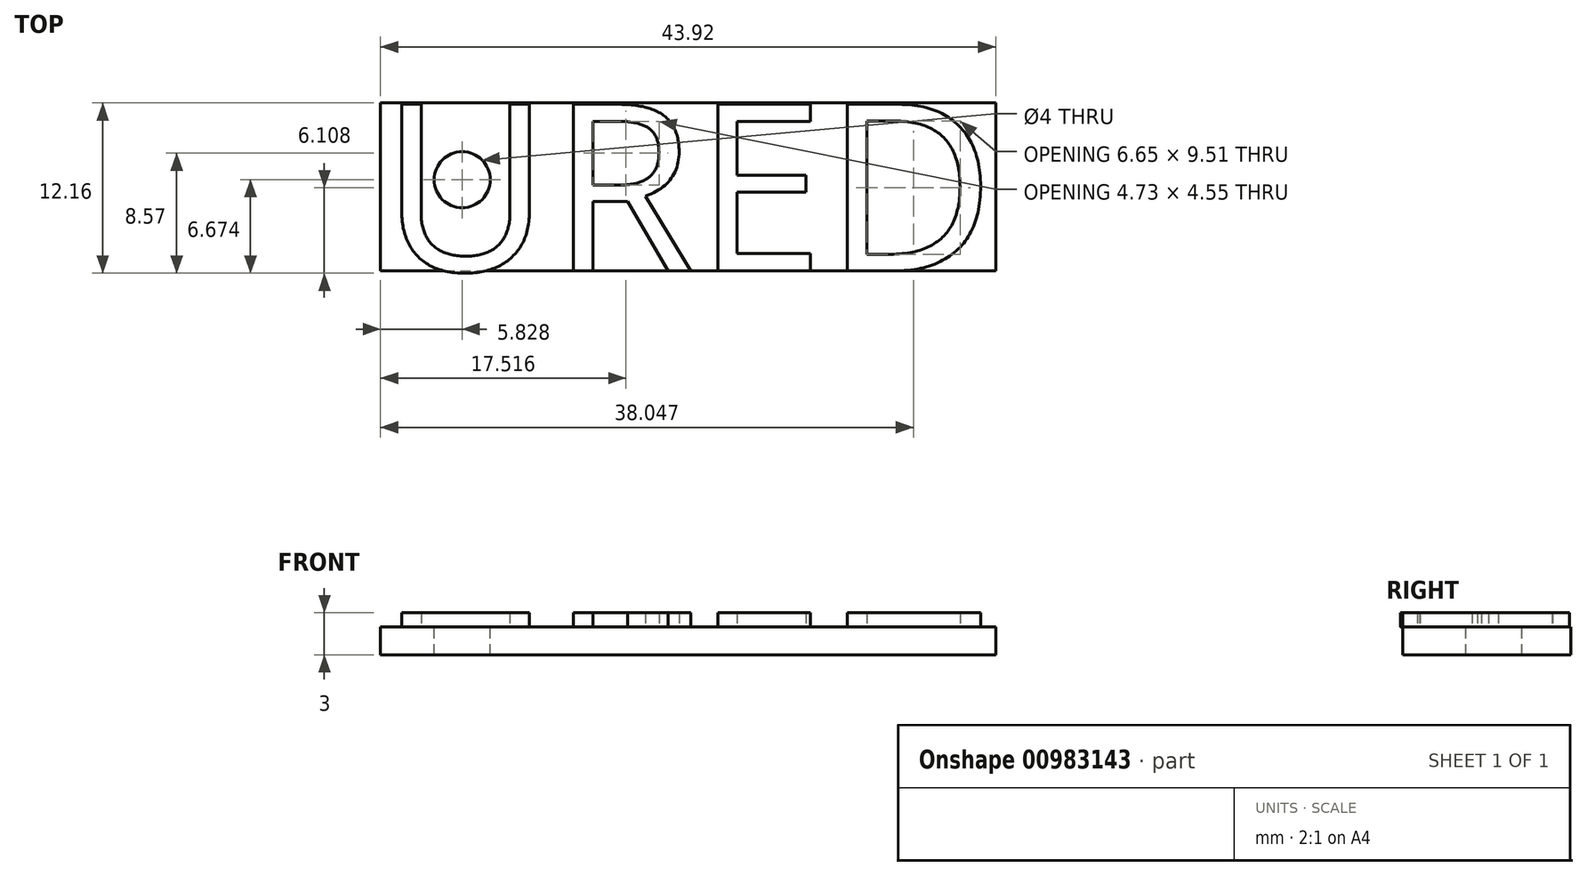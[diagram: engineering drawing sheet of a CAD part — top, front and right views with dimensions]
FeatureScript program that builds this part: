
annotation { "Feature Type Name" : "Feature", "Feature Type Description" : "" }
export const myFeature = defineFeature(function(context is Context, id is Id, definition is map)
    precondition{}
    {
        {
            var Q0;
            Q0=qCreatedBy(makeId("Top.planeOp"),FACE);
            var sketch = newSketch(context, id + "F0", { "sketchPlane" : qUnion([Q0])});
            skText(sketch, "E0", { "text": "URED", "fontName": "OpenSans-Regular.ttf"});
            const initialGuessF0  = {"E0": [-0.0347, 0, 1, 0, 0.012]};
            skSetInitialGuess(sketch, initialGuessF0);
            skSolve(sketch);
        }
        {
            var Q0;
            Q0=qCreatedBy(makeId("Top.planeOp"),FACE);
            var sketch = newSketch(context, id + "F1", { "sketchPlane" : qUnion([Q0])});
            skLineSegment(sketch, "E1.0", {"start": v(-34.7, 12) * mm, "end": v(9.22, 12) * mm});
            skLineSegment(sketch, "E2.0", {"start": v(-34.7, 0) * mm, "end": v(-34.7, 12) * mm});
            skLineSegment(sketch, "E3.0", {"start": v(-34.7, 0) * mm, "end": v(9.22, 0) * mm});
            skLineSegment(sketch, "E4.0", {"start": v(9.22, 0) * mm, "end": v(9.22, 12) * mm});
            skSolve(sketch);
        }
        {
            var Q0;
            Q0 = qSketchRegion(id + "F0", true);
            extrude(context, id + "F2", {"entities" : qUnion([Q0]), "depth" : 1 * mm, "offsetDistance" : 25 * mm});
        }
        {
            var Q0;
            Q0 = qSketchRegion(id + "F1", true);
            extrude(context, id + "F3", {"entities" : qUnion([Q0]), "oppositeDirection" : true, "depth" : 2 * mm, "offsetDistance" : 25 * mm});
        }
        {
            var Q0;
            Q0=makeQuery(id+"F3.opExtrude","CAP_FACE",FACE,{"disambiguationData":[OSD([sQuery(id+"F1.wireOp",EDGE,"E1.0"),sQuery(id+"F1.wireOp",EDGE,"E2.0"),sQuery(id+"F1.wireOp",EDGE,"E3.0"),sQuery(id+"F1.wireOp",EDGE,"E4.0")])],"isStart":true});
            var sketch = newSketch(context, id + "F4", { "sketchPlane" : qUnion([Q0])});
            skCircle(sketch, "E5", {"center": v(-28.87, 6.51) * mm, "radius": 2 * mm});
            skSolve(sketch);
        }
        {
            var Q0;
            Q0 = qSketchRegion(id + "F4", true);
            extrude(context, id + "F5", {"entities" : qUnion([Q0]), "operationType" : NewBodyOperationType.REMOVE, "endBound" : BoundingType.THROUGH_ALL, "oppositeDirection" : true, "depth" : 25 * mm, "offsetDistance" : 25 * mm});
        }
    });
